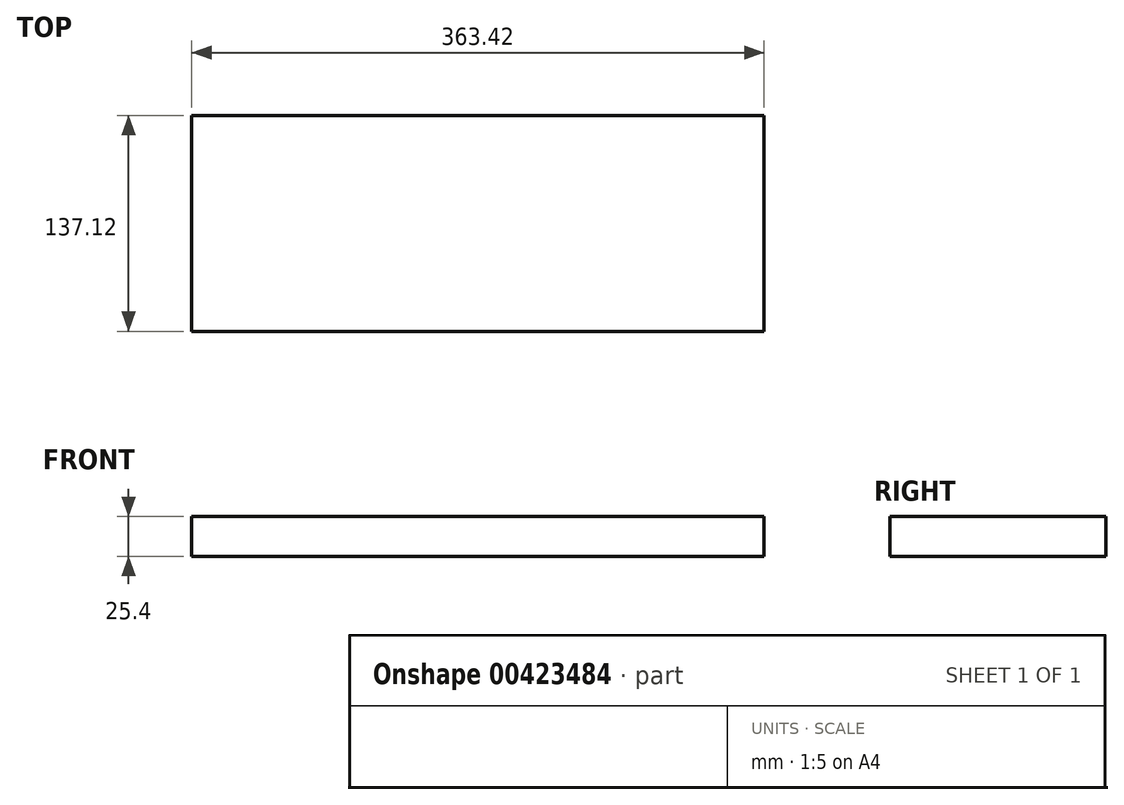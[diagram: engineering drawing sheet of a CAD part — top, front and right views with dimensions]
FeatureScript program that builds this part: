
annotation { "Feature Type Name" : "Feature", "Feature Type Description" : "" }
export const myFeature = defineFeature(function(context is Context, id is Id, definition is map)
    precondition{}
    {
        {
            var Q0;
            Q0=qCreatedBy(makeId("Top.planeOp"),FACE);
            var sketch = newSketch(context, id + "F0", { "sketchPlane" : qUnion([Q0])});
            skLineSegment(sketch, "E0.bottom", {"start": v(181.71, 92.4) * mm, "end": v(-181.71, 92.4) * mm});
            skLineSegment(sketch, "E0.top", {"start": v(181.71, -44.72) * mm, "end": v(-181.71, -44.72) * mm});
            skLineSegment(sketch, "E0.left", {"start": v(181.71, 92.4) * mm, "end": v(181.71, -44.72) * mm});
            skLineSegment(sketch, "E0.right", {"start": v(-181.71, 92.4) * mm, "end": v(-181.71, -44.72) * mm});
            skPoint(sketch, "E0.middle", {"position": v(0, 23.84) * mm});
            skSolve(sketch);
        }
        {
            var Q0;
            Q0=makeQuery(id+"F0.imprint","IMPRINT",FACE,{"disambiguationData":[TD([[makeQuery(id+"F0.imprint","IMPRINT",EDGE,{"derivedFrom":sQuery(id+"F0.wireOp",EDGE,"E0.bottom")}),1.0]])]});
            extrude(context, id + "F1", {"entities" : qUnion([Q0]), "depth" : 25.4 * mm});
        }
    });
